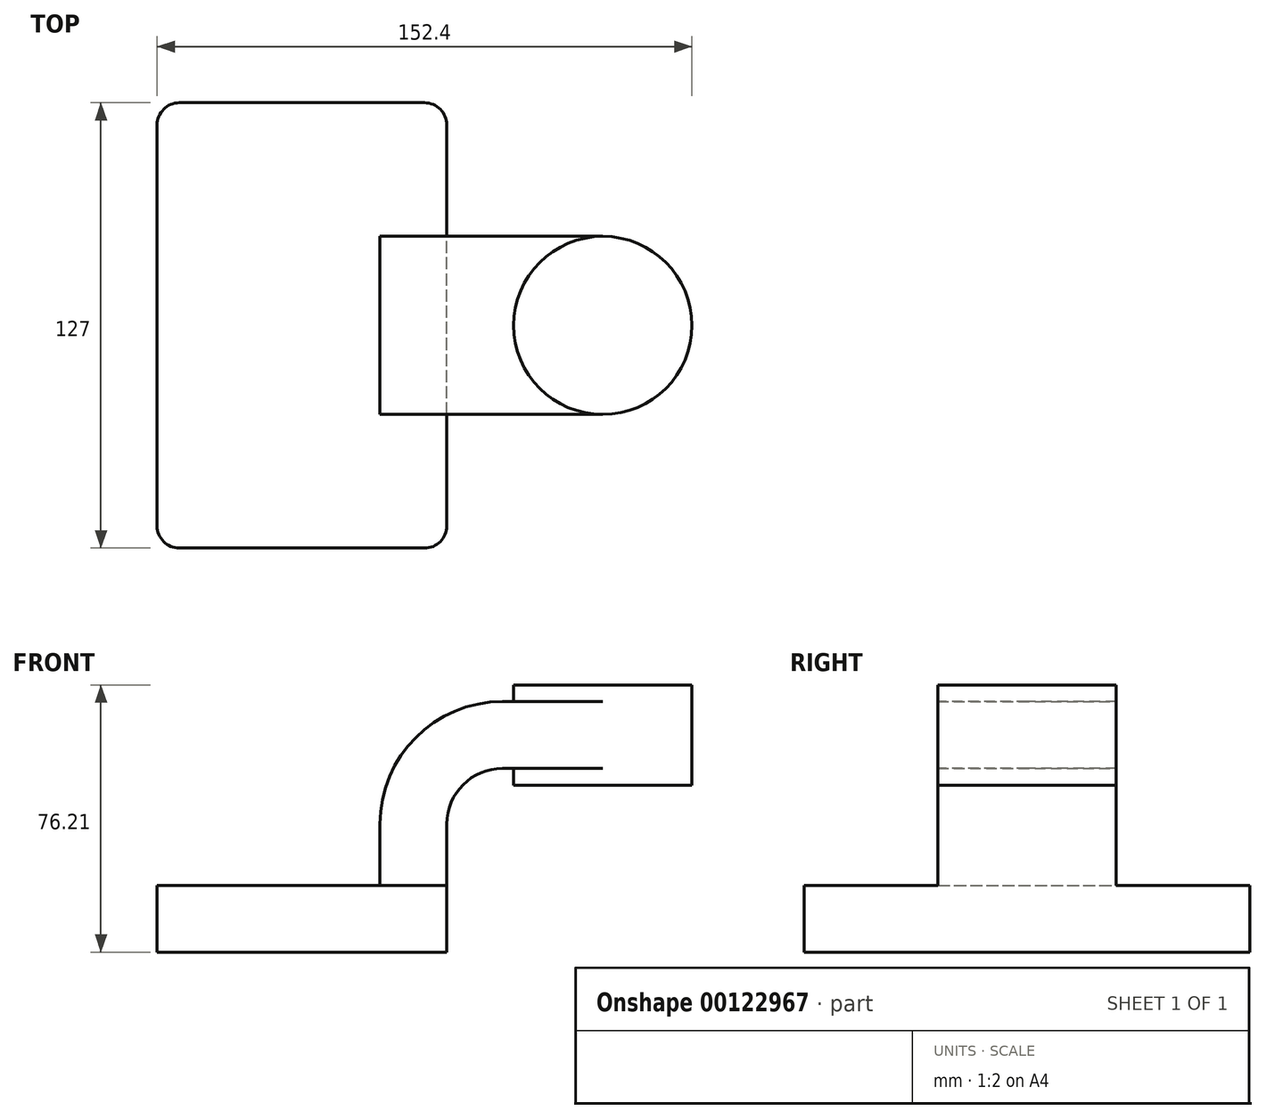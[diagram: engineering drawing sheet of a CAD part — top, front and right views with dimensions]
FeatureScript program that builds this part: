
annotation { "Feature Type Name" : "Feature", "Feature Type Description" : "" }
export const myFeature = defineFeature(function(context is Context, id is Id, definition is map)
    precondition{}
    {
        {
            var Q0;
            Q0=qCreatedBy(makeId("Front.planeOp"),FACE);
            var sketch = newSketch(context, id + "F0", { "sketchPlane" : qUnion([Q0])});
            skLineSegment(sketch, "E0.bottom", {"start": v(41.27, 9.53) * mm, "end": v(-41.28, 9.53) * mm});
            skLineSegment(sketch, "E0.top", {"start": v(41.28, -9.53) * mm, "end": v(-41.27, -9.53) * mm});
            skLineSegment(sketch, "E0.left", {"start": v(41.28, 9.53) * mm, "end": v(41.28, -9.52) * mm});
            skLineSegment(sketch, "E0.right", {"start": v(-41.28, 9.53) * mm, "end": v(-41.28, -9.52) * mm});
            skPoint(sketch, "E0.middle", {"position": v(0, 0) * mm});
            skLineSegment(sketch, "E1.bottom", {"start": v(111.13, 38.1) * mm, "end": v(60.33, 38.1) * mm});
            skLineSegment(sketch, "E1.top", {"start": v(111.13, 66.67) * mm, "end": v(60.33, 66.67) * mm});
            skLineSegment(sketch, "E1.left", {"start": v(111.13, 38.1) * mm, "end": v(111.13, 66.68) * mm});
            skLineSegment(sketch, "E1.right", {"start": v(60.33, 38.1) * mm, "end": v(60.33, 66.68) * mm});
            skPoint(sketch, "E1.middle", {"position": v(85.73, 52.39) * mm});
            skLineSegment(sketch, "E2", {"start": v(41.28, 9.53) * mm, "end": v(41.28, 26.99) * mm});
            skArc(sketch, "E3", {"start": v(41.27, 26.99) * mm, "mid": v(45.92, 38.21) * mm, "end": v(57.15, 42.86) * mm});
            skLineSegment(sketch, "E4", {"start": v(57.15, 42.86) * mm, "end": v(85.73, 42.86) * mm});
            skLineSegment(sketch, "E5.0", {"start": v(57.15, 61.91) * mm, "end": v(85.73, 61.91) * mm});
            skArc(sketch, "E5.1", {"start": v(22.23, 26.99) * mm, "mid": v(32.45, 51.68) * mm, "end": v(57.15, 61.91) * mm});
            skLineSegment(sketch, "E5.2", {"start": v(22.23, 9.53) * mm, "end": v(22.23, 26.99) * mm});
            skLineSegment(sketch, "E6", {"start": v(85.73, 38.1) * mm, "end": v(85.73, 66.68) * mm});
            skFitSpline(sketch, "E7", {"points": [v(-41.28, 9.53) * mm, v(57.15, 61.91) * mm], "startDerivative": vector(0, 73.44) * mm, "endDerivative": vector(93.42, 0) * mm});
            skSolve(sketch);
        }
        {
            var Q0;
            Q0=makeQuery(id+"F0.imprint","IMPRINT",FACE,{"disambiguationData":[TD([[makeQuery(id+"F0.imprint","IMPRINT",EDGE,{"derivedFrom":sQuery(id+"F0.wireOp",EDGE,"E0.bottom")}),1.0]])]});
            extrude(context, id + "F1", {"entities" : qUnion([Q0]), "endBound" : BoundingType.SYMMETRIC, "depth" : 127 * mm});
        }
        {
            var Q0;
            {var subQ1=sQuery(id+"F0.wireOp",EDGE,"E2");Q0=makeQuery(id+"F0.imprint","IMPRINT",FACE,{"disambiguationData":[TD([[makeQuery(id+"F0.imprint","IMPRINT",EDGE,{"derivedFrom":subQ1}),1.0]])]});}
            var Q1;
            {var subQ0=sQuery(id+"F0.wireOp",EDGE,"E4");var subQ1=sQuery(id+"F0.wireOp",EDGE,"E1.right");var subQ2=makeQuery(id+"F0.imprint","INTERSECT",VERTEX,{"derivedFrom":[subQ1,subQ0]});Q1=makeQuery(id+"F0.imprint","IMPRINT",FACE,{"disambiguationData":[TD([[makeQuery(id+"F0.imprint","IMPRINT",EDGE,{"disambiguationData":[TD([[subQ2,-1.0]])],"derivedFrom":subQ1}),-1.0]])]});}
            extrude(context, id + "F2", {"entities" : qUnion([Q0, Q1]), "operationType" : NewBodyOperationType.ADD, "endBound" : BoundingType.SYMMETRIC, "depth" : 50.8 * mm});
        }
        {
            var Q0;
            Q0=makeQuery(id+"F0.imprint","IMPRINT",FACE,{"disambiguationData":[TD([[makeQuery(id+"F0.imprint","IMPRINT",EDGE,{"derivedFrom":sQuery(id+"F0.wireOp",EDGE,"E5.1")}),1.0]])]});
            extrude(context, id + "F3", {"entities" : qUnion([Q0]), "operationType" : NewBodyOperationType.ADD, "endBound" : BoundingType.SYMMETRIC, "depth" : 15.88 * mm});
        }
        {
            var Q0;
            {var subQ0=sQuery(id+"F0.wireOp",EDGE,"E1.left");Q0=makeQuery(id+"F0.imprint","IMPRINT",FACE,{"disambiguationData":[TD([[makeQuery(id+"F0.imprint","IMPRINT",EDGE,{"derivedFrom":subQ0}),1.0]])]});}
            var Q1;
            Q1=sQuery(id+"F0.wireOp",EDGE,"E6");
            revolve(context, id + "F4", {"operationType" : NewBodyOperationType.ADD, "entities" : qUnion([Q0]), "axis" : qUnion([Q1]), "revolveType" : RevolveType.FULL});
        }
        {
            var Q0;
            Q0=makeQuery(id+"F1.opExtrude","CAP_EDGE",EDGE,{"disambiguationData":[OSD([sQuery(id+"F0.wireOp",EDGE,"E0.left")])],"isStart":false});
            var Q1;
            Q1=makeQuery(id+"F1.opExtrude","CAP_EDGE",EDGE,{"disambiguationData":[OSD([sQuery(id+"F0.wireOp",EDGE,"E0.right")])],"isStart":false});
            var Q2;
            Q2=makeQuery(id+"F1.opExtrude","CAP_EDGE",EDGE,{"disambiguationData":[OSD([sQuery(id+"F0.wireOp",EDGE,"E0.right")])],"isStart":true});
            var Q3;
            Q3=makeQuery(id+"F1.opExtrude","CAP_EDGE",EDGE,{"disambiguationData":[OSD([sQuery(id+"F0.wireOp",EDGE,"E0.left")])],"isStart":true});
            fillet(context, id + "F5", {"entities" : qUnion([Q0, Q1, Q2, Q3]), "radius" : 6.35 * mm, "tangentPropagation" : true, "allowEdgeOverflow" : false});
        }
    });
